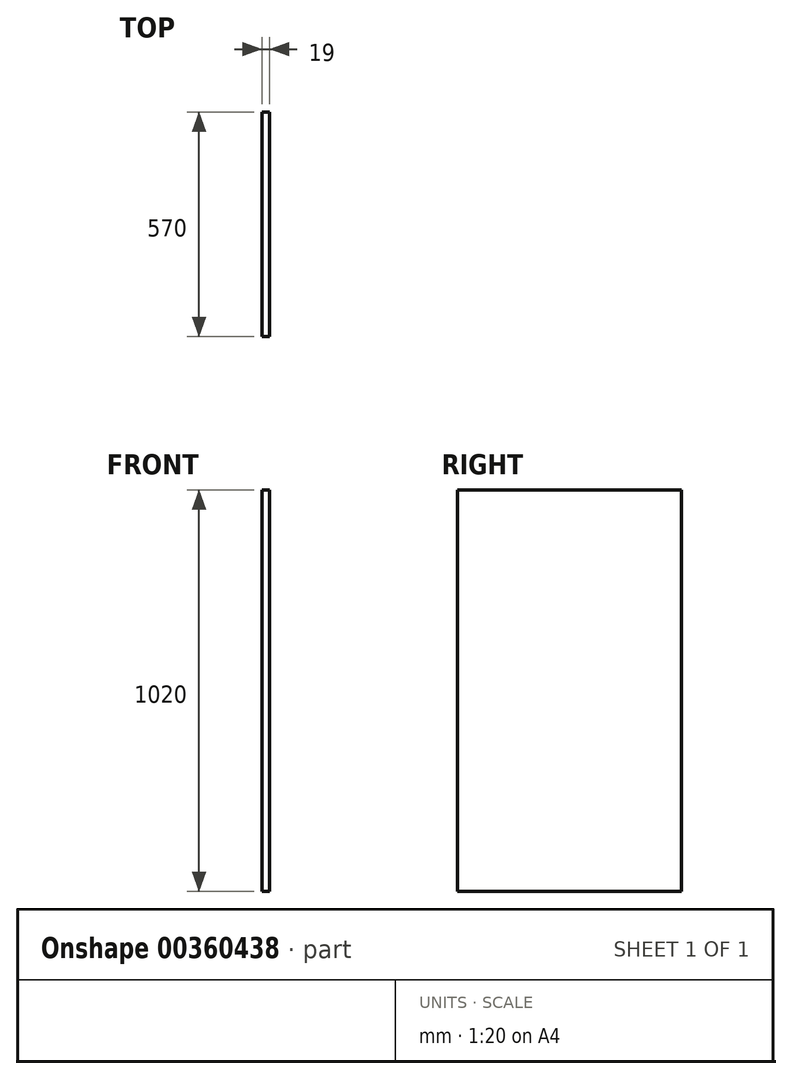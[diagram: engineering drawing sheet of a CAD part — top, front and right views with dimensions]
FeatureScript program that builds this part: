
annotation { "Feature Type Name" : "Feature", "Feature Type Description" : "" }
export const myFeature = defineFeature(function(context is Context, id is Id, definition is map)
    precondition{}
    {
        {
            var Q0;
            Q0=qCreatedBy(makeId("Right.planeOp"),FACE);
            var sketch = newSketch(context, id + "F0", { "sketchPlane" : qUnion([Q0])});
            skLineSegment(sketch, "E0.bottom", {"start": v(570, 1020) * mm, "end": v(0, 1020) * mm});
            skLineSegment(sketch, "E0.top", {"start": v(570, 0) * mm, "end": v(0, 0) * mm});
            skLineSegment(sketch, "E0.left", {"start": v(570, 1020) * mm, "end": v(570, 0) * mm});
            skLineSegment(sketch, "E0.right", {"start": v(0, 1020) * mm, "end": v(0, 0) * mm});
            skSolve(sketch);
        }
        {
            var Q0;
            Q0=makeQuery(id+"F0.imprint","IMPRINT",FACE,{"disambiguationData":[TD([[makeQuery(id+"F0.imprint","IMPRINT",EDGE,{"derivedFrom":sQuery(id+"F0.wireOp",EDGE,"E0.bottom")}),1.0]])]});
            extrude(context, id + "F1", {"entities" : qUnion([Q0]), "depth" : 19 * mm});
        }
    });
